# Revit family: 824b77e3-f2cf-4587-95cb-8e550c2abeb6
name_source: partatom
category: Plumbing Fixtures
revit_build: Autodesk Revit Architecture 2014 (Build: 20131024_2115(x64)
units: mm (PartAtom-declared; Revit-internal decimal feet)

## types (3) — shared parameters
Assembly Code = D2010400
CW Connection = No
CWFU = 1
Celite: Categoria = Cozinha
Celite: Cores Disponíveis = Cromado
Celite: Código = B5008I9CR3
Celite: Descrição = Torneira de mesa para cozinha (B5008I9CR3), linha Incepa Zip - Metais Incepa
Celite: Fabricante = Incepa
Celite: Linha = Zip
Celite: Norma = ABNT NBR 15748:2009 - Requisitos e métodos de ensaio
Celite: Produto = Metais
Celite: Versão = Autodesk Revit MEP 2014
Description = Torneira de mesa para cozinha (B5008I9CR3), linha Incepa Zip - Metais Incepa
Desenvolvido por = ofcdesk
Diâmetro Água Fria = 20 mm
HW Connection = No
Incepa: Tipo = Torneiras
Manufacturer = Incepa
Model = B5008I9CR3
Raio Água Fria = 10 mm
Selo de Qualidade ofcdesk = Standard
URL = http://www.incepa.com.br
Vent Connection = No
Waste Connection = No
zero-valued in all types: Cost, Default Elevation, HWFU, WFU

## type names (no varying parameters)
- Bica alta - com flexível 300mm
- Bica alta - com flexível 400mm
- Bica alta - sem flexível

## geometry (parser evidence)
native form markers: Blend x2, Sweep x2
no freeform markers — native parametric forms only
